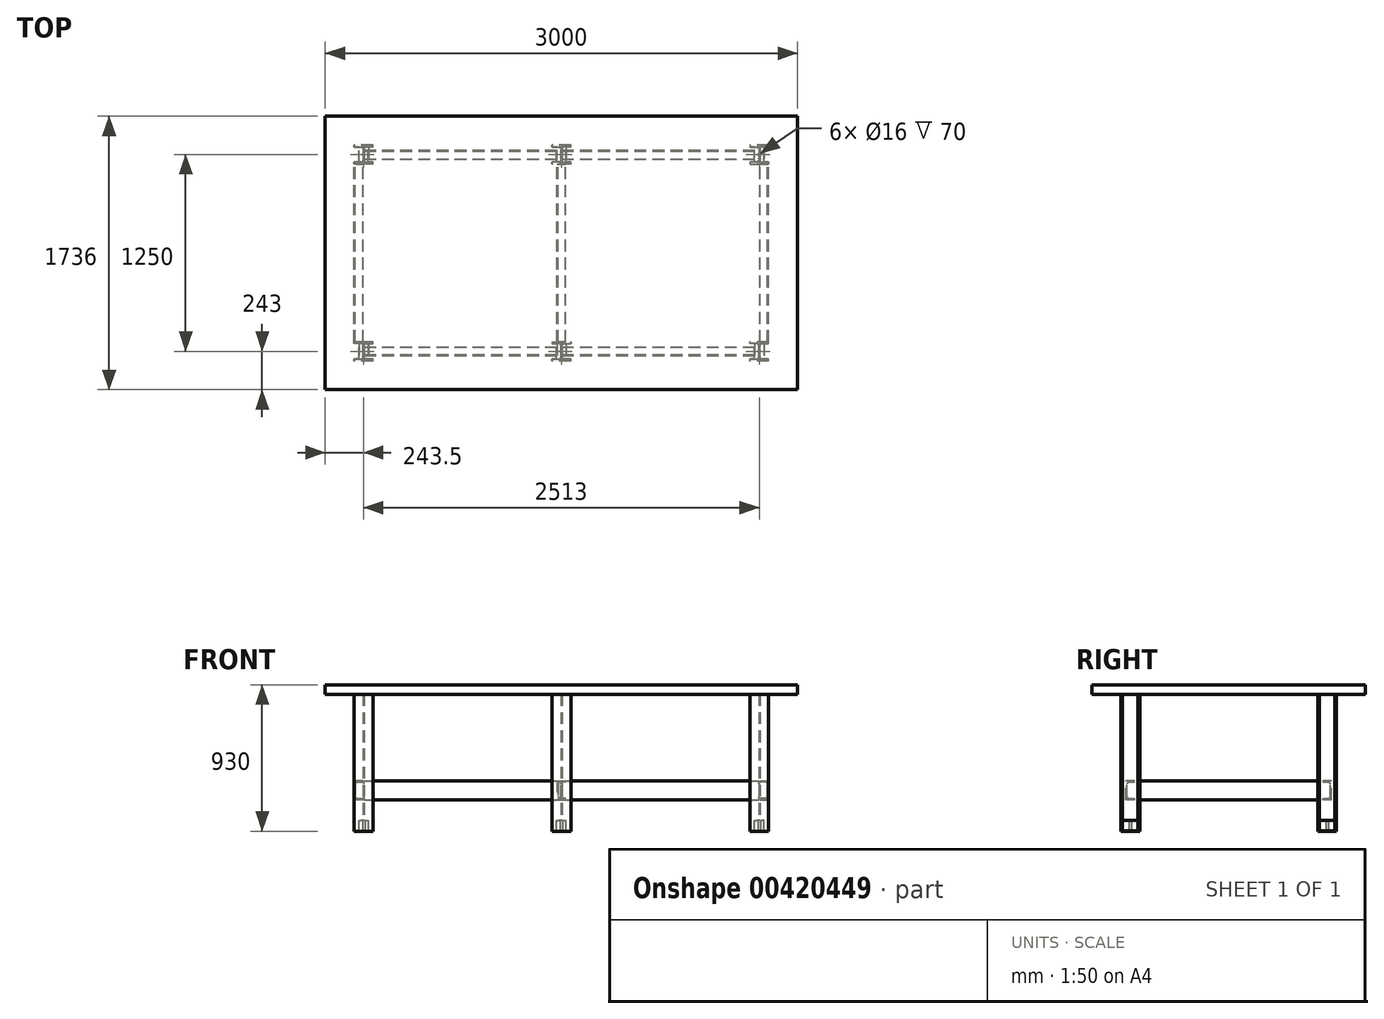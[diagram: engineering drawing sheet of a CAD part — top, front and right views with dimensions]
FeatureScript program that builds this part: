
annotation { "Feature Type Name" : "Feature", "Feature Type Description" : "" }
export const myFeature = defineFeature(function(context is Context, id is Id, definition is map)
    precondition{}
    {
        {
            var Q0;
            Q0=qCreatedBy(makeId("Top.planeOp"),FACE);
            var sketch = newSketch(context, id + "F0", { "sketchPlane" : qUnion([Q0])});
            skLineSegment(sketch, "E0", {"start": v(0, 60) * mm, "end": v(60, 60) * mm});
            skLineSegment(sketch, "E1", {"start": v(60, 60) * mm, "end": v(60, 49) * mm});
            skLineSegment(sketch, "E2", {"start": v(60, 49) * mm, "end": v(15.75, 49) * mm});
            skLineSegment(sketch, "E3", {"start": v(3.25, 36.5) * mm, "end": v(3.25, -36.5) * mm});
            skLineSegment(sketch, "E4", {"start": v(15.75, -49) * mm, "end": v(60, -49) * mm});
            skLineSegment(sketch, "E5", {"start": v(60, -49) * mm, "end": v(60, -60) * mm});
            skLineSegment(sketch, "E6", {"start": v(60, -60) * mm, "end": v(0, -60) * mm});
            skPoint(sketch, "E7.visualSharp", {"position": v(3.25, 49) * mm});
            skArc(sketch, "E7.filletArc", {"start": v(15.75, 49) * mm, "mid": v(6.91, 45.34) * mm, "end": v(3.25, 36.5) * mm});
            skPoint(sketch, "E8.visualSharp", {"position": v(3.25, -49) * mm});
            skArc(sketch, "E8.filletArc", {"start": v(3.25, -36.5) * mm, "mid": v(6.91, -45.34) * mm, "end": v(15.75, -49) * mm});
            skLineSegment(sketch, "E9.MirrorCS", {"start": v(0, 60) * mm, "end": v(-60, 60) * mm});
            skLineSegment(sketch, "E10.MirrorCS", {"start": v(-60, 60) * mm, "end": v(-60, 49) * mm});
            skPoint(sketch, "E11.MirrorP", {"position": v(-3.25, -49) * mm});
            skLineSegment(sketch, "E12.MirrorCS", {"start": v(-60, 49) * mm, "end": v(-15.75, 49) * mm});
            skLineSegment(sketch, "E13.MirrorCS", {"start": v(-3.25, 36.5) * mm, "end": v(-3.25, -36.5) * mm});
            skLineSegment(sketch, "E14.MirrorCS", {"start": v(-60, -49) * mm, "end": v(-60, -60) * mm});
            skLineSegment(sketch, "E15.MirrorCS", {"start": v(-60, -60) * mm, "end": v(0, -60) * mm});
            skArc(sketch, "E16.MirrorCS", {"start": v(-3.25, -36.5) * mm, "mid": v(-6.91, -45.34) * mm, "end": v(-15.75, -49) * mm});
            skLineSegment(sketch, "E17.MirrorCS", {"start": v(-15.75, -49) * mm, "end": v(-60, -49) * mm});
            skArc(sketch, "E18.MirrorCS", {"start": v(-15.75, 49) * mm, "mid": v(-6.91, 45.34) * mm, "end": v(-3.25, 36.5) * mm});
            skPoint(sketch, "E19.MirrorP", {"position": v(-3.25, 49) * mm});
            skLineSegment(sketch, "E20", {"start": v(-3.25, 0) * mm, "end": v(-1253.25, 0) * mm, "construction": true});
            skLineSegment(sketch, "E21.bottom", {"start": v(-2756.5, -1625) * mm, "end": v(243.5, -1625) * mm, "construction": true});
            skLineSegment(sketch, "E21.top", {"start": v(-2756.5, 375) * mm, "end": v(243.5, 375) * mm, "construction": true});
            skLineSegment(sketch, "E21.left", {"start": v(-2756.5, -1625) * mm, "end": v(-2756.5, 375) * mm, "construction": true});
            skLineSegment(sketch, "E21.right", {"start": v(243.5, -1625) * mm, "end": v(243.5, 375) * mm, "construction": true});
            skLineSegment(sketch, "E22", {"start": v(-628.25, 107.52) * mm, "end": v(-628.25, 0) * mm, "construction": true});
            skArc(sketch, "E23.MirrorCS", {"start": v(-1240.75, 49) * mm, "mid": v(-1249.59, 45.34) * mm, "end": v(-1253.25, 36.5) * mm});
            skArc(sketch, "E24.MirrorCS", {"start": v(-1272.25, 49) * mm, "mid": v(-1263.41, 45.34) * mm, "end": v(-1259.75, 36.5) * mm});
            skArc(sketch, "E25.MirrorCS", {"start": v(-1259.75, -36.5) * mm, "mid": v(-1263.41, -45.34) * mm, "end": v(-1272.25, -49) * mm});
            skLineSegment(sketch, "E26.MirrorCS", {"start": v(-1272.25, -49) * mm, "end": v(-1316.5, -49) * mm});
            skLineSegment(sketch, "E27.MirrorCS", {"start": v(-1256.5, 60) * mm, "end": v(-1316.5, 60) * mm});
            skLineSegment(sketch, "E28.MirrorCS", {"start": v(-1316.5, -49) * mm, "end": v(-1316.5, -60) * mm});
            skArc(sketch, "E29.MirrorCS", {"start": v(-1253.25, -36.5) * mm, "mid": v(-1249.59, -45.34) * mm, "end": v(-1240.75, -49) * mm});
            skLineSegment(sketch, "E30.MirrorCS", {"start": v(-1316.5, -60) * mm, "end": v(-1256.5, -60) * mm});
            skLineSegment(sketch, "E31.MirrorCS", {"start": v(-1316.5, 49) * mm, "end": v(-1272.25, 49) * mm});
            skLineSegment(sketch, "E32.MirrorCS", {"start": v(-1316.5, 60) * mm, "end": v(-1316.5, 49) * mm});
            skLineSegment(sketch, "E33.MirrorCS", {"start": v(-1196.5, -60) * mm, "end": v(-1256.5, -60) * mm});
            skLineSegment(sketch, "E34.MirrorCS", {"start": v(-1196.5, -49) * mm, "end": v(-1196.5, -60) * mm});
            skLineSegment(sketch, "E35.MirrorCS", {"start": v(-1240.75, -49) * mm, "end": v(-1196.5, -49) * mm});
            skLineSegment(sketch, "E36.MirrorCS", {"start": v(-1253.25, 36.5) * mm, "end": v(-1253.25, -36.5) * mm});
            skLineSegment(sketch, "E37.MirrorCS", {"start": v(-1196.5, 49) * mm, "end": v(-1240.75, 49) * mm});
            skLineSegment(sketch, "E38.MirrorCS", {"start": v(-1196.5, 60) * mm, "end": v(-1196.5, 49) * mm});
            skLineSegment(sketch, "E39.MirrorCS", {"start": v(-1256.5, 60) * mm, "end": v(-1196.5, 60) * mm});
            skLineSegment(sketch, "E40.MirrorCS", {"start": v(-1259.75, 36.5) * mm, "end": v(-1259.75, -36.5) * mm});
            skPoint(sketch, "E41.MirrorP", {"position": v(-1259.75, 49) * mm});
            skLineSegment(sketch, "E42.MirrorCS", {"start": v(-1253.25, 0) * mm, "end": v(-3.25, 0) * mm, "construction": true});
            skPoint(sketch, "E43.MirrorP", {"position": v(-1253.25, 49) * mm});
            skPoint(sketch, "E44.MirrorP", {"position": v(-1253.25, -49) * mm});
            skPoint(sketch, "E45.MirrorP", {"position": v(-1259.75, -49) * mm});
            skLineSegment(sketch, "E46", {"start": v(-1259.75, 0) * mm, "end": v(-2509.75, 0) * mm, "construction": true});
            skPoint(sketch, "E46.endSnap0", {"position": v(-1259.75, 0) * mm});
            skLineSegment(sketch, "E47", {"start": v(-1884.75, 66.72) * mm, "end": v(-1884.75, 0) * mm, "construction": true});
            skPoint(sketch, "E47.endSnap0", {"position": v(-1884.75, 0) * mm});
            skArc(sketch, "E48.MirrorCS", {"start": v(-2516.25, -36.5) * mm, "mid": v(-2519.91, -45.34) * mm, "end": v(-2528.75, -49) * mm});
            skArc(sketch, "E49.MirrorCS", {"start": v(-2509.75, -36.5) * mm, "mid": v(-2506.09, -45.34) * mm, "end": v(-2497.25, -49) * mm});
            skArc(sketch, "E50.MirrorCS", {"start": v(-2528.75, 49) * mm, "mid": v(-2519.91, 45.34) * mm, "end": v(-2516.25, 36.5) * mm});
            skLineSegment(sketch, "E51.MirrorCS", {"start": v(-2516.25, 36.5) * mm, "end": v(-2516.25, -36.5) * mm});
            skLineSegment(sketch, "E52.MirrorCS", {"start": v(-2509.75, 36.5) * mm, "end": v(-2509.75, -36.5) * mm});
            skArc(sketch, "E53.MirrorCS", {"start": v(-2497.25, 49) * mm, "mid": v(-2506.09, 45.34) * mm, "end": v(-2509.75, 36.5) * mm});
            skLineSegment(sketch, "E54.MirrorCS", {"start": v(-2497.25, -49) * mm, "end": v(-2453, -49) * mm});
            skLineSegment(sketch, "E55.MirrorCS", {"start": v(-2453, 49) * mm, "end": v(-2497.25, 49) * mm});
            skLineSegment(sketch, "E56.MirrorCS", {"start": v(-2453, -49) * mm, "end": v(-2453, -60) * mm});
            skLineSegment(sketch, "E57.MirrorCS", {"start": v(-2513, 60) * mm, "end": v(-2453, 60) * mm});
            skLineSegment(sketch, "E58.MirrorCS", {"start": v(-2513, 60) * mm, "end": v(-2573, 60) * mm});
            skLineSegment(sketch, "E59.MirrorCS", {"start": v(-2453, 60) * mm, "end": v(-2453, 49) * mm});
            skPoint(sketch, "E60.MirrorP", {"position": v(-2509.75, 0) * mm});
            skLineSegment(sketch, "E61.MirrorCS", {"start": v(-2453, -60) * mm, "end": v(-2513, -60) * mm});
            skLineSegment(sketch, "E62.MirrorCS", {"start": v(-2573, 49) * mm, "end": v(-2528.75, 49) * mm});
            skLineSegment(sketch, "E63.MirrorCS", {"start": v(-2573, 60) * mm, "end": v(-2573, 49) * mm});
            skLineSegment(sketch, "E64.MirrorCS", {"start": v(-2573, -60) * mm, "end": v(-2513, -60) * mm});
            skLineSegment(sketch, "E65.MirrorCS", {"start": v(-2573, -49) * mm, "end": v(-2573, -60) * mm});
            skLineSegment(sketch, "E66.MirrorCS", {"start": v(-2528.75, -49) * mm, "end": v(-2573, -49) * mm});
            skPoint(sketch, "E67.MirrorP", {"position": v(-2516.25, 49) * mm});
            skPoint(sketch, "E68.MirrorP", {"position": v(-2516.25, -49) * mm});
            skPoint(sketch, "E69.MirrorP", {"position": v(-2509.75, 49) * mm});
            skLineSegment(sketch, "E70.MirrorCS", {"start": v(-2509.75, 0) * mm, "end": v(-1259.75, 0) * mm, "construction": true});
            skPoint(sketch, "E71.MirrorP", {"position": v(-2509.75, -49) * mm});
            skLineSegment(sketch, "E72", {"start": v(-2573, -60) * mm, "end": v(-2573, -158.37) * mm, "construction": true});
            skLineSegment(sketch, "E73", {"start": v(-2573, -158.37) * mm, "end": v(60, -158.37) * mm, "construction": true});
            skLineSegment(sketch, "E74", {"start": v(60, -158.37) * mm, "end": v(60, -60) * mm, "construction": true});
            skLineSegment(sketch, "E75", {"start": v(-1256.5, -158.37) * mm, "end": v(-1256.5, -1625) * mm, "construction": true});
            skLineSegment(sketch, "E76", {"start": v(-2756.5, -625) * mm, "end": v(243.5, -625) * mm, "construction": true});
            skLineSegment(sketch, "E77.MirrorCS", {"start": v(-1253.25, -1286.5) * mm, "end": v(-1253.25, -1213.5) * mm});
            skLineSegment(sketch, "E78.MirrorCS", {"start": v(-1256.5, -1310) * mm, "end": v(-1196.5, -1310) * mm});
            skLineSegment(sketch, "E79.MirrorCS", {"start": v(-1196.5, -1299) * mm, "end": v(-1240.75, -1299) * mm});
            skArc(sketch, "E80.MirrorCS", {"start": v(-1259.75, -1213.5) * mm, "mid": v(-1263.41, -1204.66) * mm, "end": v(-1272.25, -1201) * mm});
            skArc(sketch, "E81.MirrorCS", {"start": v(-1240.75, -1299) * mm, "mid": v(-1249.59, -1295.34) * mm, "end": v(-1253.25, -1286.5) * mm});
            skArc(sketch, "E82.MirrorCS", {"start": v(-1253.25, -1213.5) * mm, "mid": v(-1249.59, -1204.66) * mm, "end": v(-1240.75, -1201) * mm});
            skLineSegment(sketch, "E83.MirrorCS", {"start": v(-1259.75, -1286.5) * mm, "end": v(-1259.75, -1213.5) * mm});
            skArc(sketch, "E84.MirrorCS", {"start": v(-1272.25, -1299) * mm, "mid": v(-1263.41, -1295.34) * mm, "end": v(-1259.75, -1286.5) * mm});
            skLineSegment(sketch, "E85.MirrorCS", {"start": v(-1196.5, -1190) * mm, "end": v(-1256.5, -1190) * mm});
            skLineSegment(sketch, "E86.MirrorCS", {"start": v(-1240.75, -1201) * mm, "end": v(-1196.5, -1201) * mm});
            skArc(sketch, "E87.MirrorCS", {"start": v(15.75, -1299) * mm, "mid": v(6.91, -1295.34) * mm, "end": v(3.25, -1286.5) * mm});
            skLineSegment(sketch, "E88.MirrorCS", {"start": v(0, -1310) * mm, "end": v(-60, -1310) * mm});
            skLineSegment(sketch, "E89.MirrorCS", {"start": v(-60, -1310) * mm, "end": v(-60, -1299) * mm});
            skLineSegment(sketch, "E90.MirrorCS", {"start": v(-60, -1201) * mm, "end": v(-60, -1190) * mm});
            skArc(sketch, "E91.MirrorCS", {"start": v(-3.25, -1213.5) * mm, "mid": v(-6.91, -1204.66) * mm, "end": v(-15.75, -1201) * mm});
            skLineSegment(sketch, "E92.MirrorCS", {"start": v(0, -1310) * mm, "end": v(60, -1310) * mm});
            skLineSegment(sketch, "E93.MirrorCS", {"start": v(60, -1299) * mm, "end": v(15.75, -1299) * mm});
            skLineSegment(sketch, "E94.MirrorCS", {"start": v(3.25, -1286.5) * mm, "end": v(3.25, -1213.5) * mm});
            skArc(sketch, "E95.MirrorCS", {"start": v(-15.75, -1299) * mm, "mid": v(-6.91, -1295.34) * mm, "end": v(-3.25, -1286.5) * mm});
            skArc(sketch, "E96.MirrorCS", {"start": v(-2516.25, -1213.5) * mm, "mid": v(-2519.91, -1204.66) * mm, "end": v(-2528.75, -1201) * mm});
            skLineSegment(sketch, "E97.MirrorCS", {"start": v(-3.25, -1286.5) * mm, "end": v(-3.25, -1213.5) * mm});
            skArc(sketch, "E98.MirrorCS", {"start": v(-2509.75, -1213.5) * mm, "mid": v(-2506.09, -1204.66) * mm, "end": v(-2497.25, -1201) * mm});
            skArc(sketch, "E99.MirrorCS", {"start": v(-2528.75, -1299) * mm, "mid": v(-2519.91, -1295.34) * mm, "end": v(-2516.25, -1286.5) * mm});
            skLineSegment(sketch, "E100.MirrorCS", {"start": v(-60, -1299) * mm, "end": v(-15.75, -1299) * mm});
            skLineSegment(sketch, "E101.MirrorCS", {"start": v(-15.75, -1201) * mm, "end": v(-60, -1201) * mm});
            skLineSegment(sketch, "E102.MirrorCS", {"start": v(-2453, -1190) * mm, "end": v(-2513, -1190) * mm});
            skArc(sketch, "E103.MirrorCS", {"start": v(3.25, -1213.5) * mm, "mid": v(6.91, -1204.66) * mm, "end": v(15.75, -1201) * mm});
            skLineSegment(sketch, "E104.MirrorCS", {"start": v(-2516.25, -1286.5) * mm, "end": v(-2516.25, -1213.5) * mm});
            skLineSegment(sketch, "E105.MirrorCS", {"start": v(-1256.5, -1310) * mm, "end": v(-1316.5, -1310) * mm});
            skLineSegment(sketch, "E106.MirrorCS", {"start": v(-2497.25, -1201) * mm, "end": v(-2453, -1201) * mm});
            skLineSegment(sketch, "E107.MirrorCS", {"start": v(-2573, -1201) * mm, "end": v(-2573, -1190) * mm});
            skLineSegment(sketch, "E108.MirrorCS", {"start": v(-1272.25, -1201) * mm, "end": v(-1316.5, -1201) * mm});
            skLineSegment(sketch, "E109.MirrorCS", {"start": v(-2513, -1310) * mm, "end": v(-2453, -1310) * mm});
            skLineSegment(sketch, "E110.MirrorCS", {"start": v(-60, -1190) * mm, "end": v(0, -1190) * mm});
            skLineSegment(sketch, "E111.MirrorCS", {"start": v(-2509.75, -1286.5) * mm, "end": v(-2509.75, -1213.5) * mm});
            skLineSegment(sketch, "E112.MirrorCS", {"start": v(15.75, -1201) * mm, "end": v(60, -1201) * mm});
            skLineSegment(sketch, "E113.MirrorCS", {"start": v(-2573, -1299) * mm, "end": v(-2528.75, -1299) * mm});
            skLineSegment(sketch, "E114.MirrorCS", {"start": v(60, -1190) * mm, "end": v(0, -1190) * mm});
            skLineSegment(sketch, "E115.MirrorCS", {"start": v(-1316.5, -1299) * mm, "end": v(-1272.25, -1299) * mm});
            skArc(sketch, "E116.MirrorCS", {"start": v(-2497.25, -1299) * mm, "mid": v(-2506.09, -1295.34) * mm, "end": v(-2509.75, -1286.5) * mm});
            skLineSegment(sketch, "E117.MirrorCS", {"start": v(-2573, -1190) * mm, "end": v(-2513, -1190) * mm});
            skLineSegment(sketch, "E118.MirrorCS", {"start": v(-1316.5, -1201) * mm, "end": v(-1316.5, -1190) * mm});
            skLineSegment(sketch, "E119.MirrorCS", {"start": v(-2453, -1299) * mm, "end": v(-2497.25, -1299) * mm});
            skLineSegment(sketch, "E120.MirrorCS", {"start": v(-2573, -1310) * mm, "end": v(-2573, -1299) * mm});
            skLineSegment(sketch, "E121.MirrorCS", {"start": v(-2513, -1310) * mm, "end": v(-2573, -1310) * mm});
            skLineSegment(sketch, "E122.MirrorCS", {"start": v(-1316.5, -1190) * mm, "end": v(-1256.5, -1190) * mm});
            skLineSegment(sketch, "E123.MirrorCS", {"start": v(-1316.5, -1310) * mm, "end": v(-1316.5, -1299) * mm});
            skLineSegment(sketch, "E124.MirrorCS", {"start": v(-2453, -1201) * mm, "end": v(-2453, -1190) * mm});
            skLineSegment(sketch, "E125.MirrorCS", {"start": v(-2528.75, -1201) * mm, "end": v(-2573, -1201) * mm});
            skLineSegment(sketch, "E126.MirrorCS", {"start": v(-2453, -1310) * mm, "end": v(-2453, -1299) * mm});
            skLineSegment(sketch, "E127.MirrorCS", {"start": v(60, -1201) * mm, "end": v(60, -1190) * mm});
            skLineSegment(sketch, "E128.MirrorCS", {"start": v(60, -1310) * mm, "end": v(60, -1299) * mm});
            skLineSegment(sketch, "E129.MirrorCS", {"start": v(-1196.5, -1310) * mm, "end": v(-1196.5, -1299) * mm});
            skLineSegment(sketch, "E130.MirrorCS", {"start": v(-1196.5, -1201) * mm, "end": v(-1196.5, -1190) * mm});
            skLineSegment(sketch, "E131.MirrorCS", {"start": v(-2573, -1190) * mm, "end": v(-2573, -1091.63) * mm, "construction": true});
            skLineSegment(sketch, "E132.MirrorCS", {"start": v(60, -1091.63) * mm, "end": v(60, -1190) * mm, "construction": true});
            skPoint(sketch, "E133.MirrorP", {"position": v(-1259.75, -1250) * mm});
            skPoint(sketch, "E134.MirrorP", {"position": v(-1253.25, -1201) * mm});
            skPoint(sketch, "E135.MirrorP", {"position": v(-2509.75, -1250) * mm});
            skLineSegment(sketch, "E136.MirrorCS", {"start": v(-1253.25, -1250) * mm, "end": v(-3.25, -1250) * mm, "construction": true});
            skPoint(sketch, "E137.MirrorP", {"position": v(-2509.75, -1299) * mm});
            skPoint(sketch, "E138.MirrorP", {"position": v(-1259.75, -1299) * mm});
            skPoint(sketch, "E139.MirrorP", {"position": v(3.25, -1299) * mm});
            skLineSegment(sketch, "E140.MirrorCS", {"start": v(-1259.75, -1250) * mm, "end": v(-2509.75, -1250) * mm, "construction": true});
            skPoint(sketch, "E141.MirrorP", {"position": v(-2509.75, -1201) * mm});
            skPoint(sketch, "E142.MirrorP", {"position": v(-3.25, -1299) * mm});
            skPoint(sketch, "E143.MirrorP", {"position": v(-1253.25, -1299) * mm});
            skLineSegment(sketch, "E144.MirrorCS", {"start": v(-2509.75, -1250) * mm, "end": v(-1259.75, -1250) * mm, "construction": true});
            skLineSegment(sketch, "E145.MirrorCS", {"start": v(-2573, -1091.63) * mm, "end": v(60, -1091.63) * mm, "construction": true});
            skPoint(sketch, "E146.MirrorP", {"position": v(-2516.25, -1299) * mm});
            skPoint(sketch, "E147.MirrorP", {"position": v(-2516.25, -1201) * mm});
            skLineSegment(sketch, "E148.MirrorCS", {"start": v(-628.25, -1357.52) * mm, "end": v(-628.25, -1250) * mm, "construction": true});
            skLineSegment(sketch, "E149.MirrorCS", {"start": v(-3.25, -1250) * mm, "end": v(-1253.25, -1250) * mm, "construction": true});
            skPoint(sketch, "E150.MirrorP", {"position": v(3.25, -1201) * mm});
            skLineSegment(sketch, "E151.MirrorCS", {"start": v(243.5, 375) * mm, "end": v(243.5, -1625) * mm, "construction": true});
            skLineSegment(sketch, "E152.MirrorCS", {"start": v(-1884.75, -1316.72) * mm, "end": v(-1884.75, -1250) * mm, "construction": true});
            skPoint(sketch, "E153.MirrorP", {"position": v(-3.25, -1201) * mm});
            skLineSegment(sketch, "E154.MirrorCS", {"start": v(-1256.5, -1091.63) * mm, "end": v(-1256.5, 375) * mm, "construction": true});
            skPoint(sketch, "E155.MirrorP", {"position": v(-1259.75, -1201) * mm});
            skPoint(sketch, "E156.MirrorP", {"position": v(-1884.75, -1250) * mm});
            skSolve(sketch);
        }
        {
            var Q0;
            Q0 = qSketchRegion(id + "F0", true);
            extrude(context, id + "F1", {"entities" : qUnion([Q0]), "depth" : 800 * mm});
        }
        {
            var Q0;
            Q0=makeQuery(id+"F1.opExtrude","CAP_FACE",FACE,{"disambiguationData":[OSD([sQuery(id+"F0.wireOp",EDGE,"E0"),sQuery(id+"F0.wireOp",EDGE,"E1"),sQuery(id+"F0.wireOp",EDGE,"E2"),sQuery(id+"F0.wireOp",EDGE,"E3"),sQuery(id+"F0.wireOp",EDGE,"E4"),sQuery(id+"F0.wireOp",EDGE,"E5"),sQuery(id+"F0.wireOp",EDGE,"E6"),sQuery(id+"F0.wireOp",EDGE,"E7.filletArc"),sQuery(id+"F0.wireOp",EDGE,"E8.filletArc"),sQuery(id+"F0.wireOp",EDGE,"E9.MirrorCS"),sQuery(id+"F0.wireOp",EDGE,"E10.MirrorCS"),sQuery(id+"F0.wireOp",EDGE,"E12.MirrorCS"),sQuery(id+"F0.wireOp",EDGE,"E13.MirrorCS"),sQuery(id+"F0.wireOp",EDGE,"E14.MirrorCS"),sQuery(id+"F0.wireOp",EDGE,"E15.MirrorCS"),sQuery(id+"F0.wireOp",EDGE,"E16.MirrorCS"),sQuery(id+"F0.wireOp",EDGE,"E17.MirrorCS"),sQuery(id+"F0.wireOp",EDGE,"E18.MirrorCS")])],"isStart":true});
            var sketch = newSketch(context, id + "F2", { "sketchPlane" : qUnion([Q0])});
            skLineSegment(sketch, "E157.bottom", {"start": v(-60, 60) * mm, "end": v(60, 60) * mm});
            skLineSegment(sketch, "E157.top", {"start": v(-60, 49) * mm, "end": v(60, 49) * mm});
            skLineSegment(sketch, "E157.left", {"start": v(-60, 60) * mm, "end": v(-60, 49) * mm});
            skLineSegment(sketch, "E157.right", {"start": v(60, 60) * mm, "end": v(60, 49) * mm});
            skLineSegment(sketch, "E158.bottom", {"start": v(-60, -60) * mm, "end": v(60, -60) * mm});
            skLineSegment(sketch, "E158.top", {"start": v(-60, -49) * mm, "end": v(60, -49) * mm});
            skLineSegment(sketch, "E158.left", {"start": v(-60, -60) * mm, "end": v(-60, -49) * mm});
            skLineSegment(sketch, "E158.right", {"start": v(60, -60) * mm, "end": v(60, -49) * mm});
            skSolve(sketch);
        }
        {
            var Q0;
            Q0=makeQuery(id+"F2.imprint","IMPRINT",FACE,{"disambiguationData":[TD([[makeQuery(id+"F2.imprint","IMPRINT",EDGE,{"derivedFrom":makeQuery(id+"F1.opExtrude","CAP_EDGE",EDGE,{"disambiguationData":[OSD([sQuery(id+"F0.wireOp",EDGE,"E3")])],"isStart":true})}),1.0]])]});
            var sketch = newSketch(context, id + "F3", { "sketchPlane" : qUnion([Q0])});
            skLineSegment(sketch, "E159.bottom", {"start": v(30, 49) * mm, "end": v(-30, 49) * mm});
            skLineSegment(sketch, "E159.top", {"start": v(30, -49) * mm, "end": v(-30, -49) * mm});
            skLineSegment(sketch, "E159.left", {"start": v(30, 49) * mm, "end": v(30, -49) * mm});
            skLineSegment(sketch, "E159.right", {"start": v(-30, 49) * mm, "end": v(-30, -49) * mm});
            skLineSegment(sketch, "E160.bottom", {"start": v(-1286.5, -49) * mm, "end": v(-1226.5, -49) * mm});
            skLineSegment(sketch, "E160.top", {"start": v(-1286.5, 49) * mm, "end": v(-1226.5, 49) * mm});
            skLineSegment(sketch, "E160.left", {"start": v(-1286.5, -49) * mm, "end": v(-1286.5, 49) * mm});
            skLineSegment(sketch, "E160.right", {"start": v(-1226.5, -49) * mm, "end": v(-1226.5, 49) * mm});
            skLineSegment(sketch, "E161.bottom", {"start": v(-2543, -49) * mm, "end": v(-2483, -49) * mm});
            skLineSegment(sketch, "E161.top", {"start": v(-2543, 49) * mm, "end": v(-2483, 49) * mm});
            skLineSegment(sketch, "E161.left", {"start": v(-2543, -49) * mm, "end": v(-2543, 49) * mm});
            skLineSegment(sketch, "E161.right", {"start": v(-2483, -49) * mm, "end": v(-2483, 49) * mm});
            skLineSegment(sketch, "E162.bottom", {"start": v(-2543, 1201) * mm, "end": v(-2483, 1201) * mm});
            skLineSegment(sketch, "E162.top", {"start": v(-2543, 1299) * mm, "end": v(-2483, 1299) * mm});
            skLineSegment(sketch, "E162.left", {"start": v(-2543, 1201) * mm, "end": v(-2543, 1299) * mm});
            skLineSegment(sketch, "E162.right", {"start": v(-2483, 1201) * mm, "end": v(-2483, 1299) * mm});
            skLineSegment(sketch, "E163.bottom", {"start": v(-1286.5, 1201) * mm, "end": v(-1226.5, 1201) * mm});
            skLineSegment(sketch, "E163.top", {"start": v(-1286.5, 1299) * mm, "end": v(-1226.5, 1299) * mm});
            skLineSegment(sketch, "E163.left", {"start": v(-1286.5, 1201) * mm, "end": v(-1286.5, 1299) * mm});
            skLineSegment(sketch, "E163.right", {"start": v(-1226.5, 1201) * mm, "end": v(-1226.5, 1299) * mm});
            skLineSegment(sketch, "E164.bottom", {"start": v(-30, 1201) * mm, "end": v(30, 1201) * mm});
            skLineSegment(sketch, "E164.top", {"start": v(-30, 1299) * mm, "end": v(30, 1299) * mm});
            skLineSegment(sketch, "E164.left", {"start": v(-30, 1201) * mm, "end": v(-30, 1299) * mm});
            skLineSegment(sketch, "E164.right", {"start": v(30, 1201) * mm, "end": v(30, 1299) * mm});
            skSolve(sketch);
        }
        {
            var Q0;
            Q0 = qSketchRegion(id + "F3", true);
            extrude(context, id + "F4", {"entities" : qUnion([Q0]), "depth" : 70 * mm});
        }
        {
            var Q0;
            Q0=makeQuery(id+"F2.imprint","IMPRINT",FACE,{"disambiguationData":[TD([[makeQuery(id+"F2.imprint","IMPRINT",EDGE,{"derivedFrom":sQuery(id+"F2.wireOp",EDGE,"E157.bottom")}),-1.0]])]});
            var sketch = newSketch(context, id + "F5", { "sketchPlane" : qUnion([Q0])});
            skLineSegment(sketch, "E165.bottom", {"start": v(60, -60) * mm, "end": v(-60, -60) * mm});
            skLineSegment(sketch, "E165.top", {"start": v(60, -49) * mm, "end": v(-60, -49) * mm});
            skLineSegment(sketch, "E165.left", {"start": v(60, -60) * mm, "end": v(60, -49) * mm});
            skLineSegment(sketch, "E165.right", {"start": v(-60, -60) * mm, "end": v(-60, -49) * mm});
            skLineSegment(sketch, "E166.bottom", {"start": v(60, 49) * mm, "end": v(-60, 49) * mm});
            skLineSegment(sketch, "E166.top", {"start": v(60, 60) * mm, "end": v(-60, 60) * mm});
            skLineSegment(sketch, "E166.left", {"start": v(60, 49) * mm, "end": v(60, 60) * mm});
            skLineSegment(sketch, "E166.right", {"start": v(-60, 49) * mm, "end": v(-60, 60) * mm});
            skLineSegment(sketch, "E167.bottom", {"start": v(-1196.5, 60) * mm, "end": v(-1316.5, 60) * mm});
            skLineSegment(sketch, "E167.top", {"start": v(-1196.5, 49) * mm, "end": v(-1316.5, 49) * mm});
            skLineSegment(sketch, "E167.left", {"start": v(-1196.5, 60) * mm, "end": v(-1196.5, 49) * mm});
            skLineSegment(sketch, "E167.right", {"start": v(-1316.5, 60) * mm, "end": v(-1316.5, 49) * mm});
            skLineSegment(sketch, "E168.bottom", {"start": v(-1196.5, -49) * mm, "end": v(-1316.5, -49) * mm});
            skLineSegment(sketch, "E168.top", {"start": v(-1196.5, -60) * mm, "end": v(-1316.5, -60) * mm});
            skLineSegment(sketch, "E168.left", {"start": v(-1196.5, -49) * mm, "end": v(-1196.5, -60) * mm});
            skLineSegment(sketch, "E168.right", {"start": v(-1316.5, -49) * mm, "end": v(-1316.5, -60) * mm});
            skLineSegment(sketch, "E169.bottom", {"start": v(-2453, 60) * mm, "end": v(-2573, 60) * mm});
            skLineSegment(sketch, "E169.top", {"start": v(-2453, 49) * mm, "end": v(-2573, 49) * mm});
            skLineSegment(sketch, "E169.left", {"start": v(-2453, 60) * mm, "end": v(-2453, 49) * mm});
            skLineSegment(sketch, "E169.right", {"start": v(-2573, 60) * mm, "end": v(-2573, 49) * mm});
            skLineSegment(sketch, "E170.bottom", {"start": v(-2453, -49) * mm, "end": v(-2573, -49) * mm});
            skLineSegment(sketch, "E170.top", {"start": v(-2453, -60) * mm, "end": v(-2573, -60) * mm});
            skLineSegment(sketch, "E170.left", {"start": v(-2453, -49) * mm, "end": v(-2453, -60) * mm});
            skLineSegment(sketch, "E170.right", {"start": v(-2573, -49) * mm, "end": v(-2573, -60) * mm});
            skLineSegment(sketch, "E171.bottom", {"start": v(-2453, 1310) * mm, "end": v(-2573, 1310) * mm});
            skLineSegment(sketch, "E171.top", {"start": v(-2453, 1299) * mm, "end": v(-2573, 1299) * mm});
            skLineSegment(sketch, "E171.left", {"start": v(-2453, 1310) * mm, "end": v(-2453, 1299) * mm});
            skLineSegment(sketch, "E171.right", {"start": v(-2573, 1310) * mm, "end": v(-2573, 1299) * mm});
            skLineSegment(sketch, "E172.bottom", {"start": v(-2453, 1201) * mm, "end": v(-2573, 1201) * mm});
            skLineSegment(sketch, "E172.top", {"start": v(-2453, 1190) * mm, "end": v(-2573, 1190) * mm});
            skLineSegment(sketch, "E172.left", {"start": v(-2453, 1201) * mm, "end": v(-2453, 1190) * mm});
            skLineSegment(sketch, "E172.right", {"start": v(-2573, 1201) * mm, "end": v(-2573, 1190) * mm});
            skLineSegment(sketch, "E173.bottom", {"start": v(-1196.5, 1310) * mm, "end": v(-1316.5, 1310) * mm});
            skLineSegment(sketch, "E173.top", {"start": v(-1196.5, 1299) * mm, "end": v(-1316.5, 1299) * mm});
            skLineSegment(sketch, "E173.left", {"start": v(-1196.5, 1310) * mm, "end": v(-1196.5, 1299) * mm});
            skLineSegment(sketch, "E173.right", {"start": v(-1316.5, 1310) * mm, "end": v(-1316.5, 1299) * mm});
            skLineSegment(sketch, "E174.bottom", {"start": v(60, 1310) * mm, "end": v(-60, 1310) * mm});
            skLineSegment(sketch, "E174.top", {"start": v(60, 1299) * mm, "end": v(-60, 1299) * mm});
            skLineSegment(sketch, "E174.left", {"start": v(60, 1310) * mm, "end": v(60, 1299) * mm});
            skLineSegment(sketch, "E174.right", {"start": v(-60, 1310) * mm, "end": v(-60, 1299) * mm});
            skLineSegment(sketch, "E175.bottom", {"start": v(60, 1201) * mm, "end": v(-60, 1201) * mm});
            skLineSegment(sketch, "E175.top", {"start": v(60, 1190) * mm, "end": v(-60, 1190) * mm});
            skLineSegment(sketch, "E175.left", {"start": v(60, 1201) * mm, "end": v(60, 1190) * mm});
            skLineSegment(sketch, "E175.right", {"start": v(-60, 1201) * mm, "end": v(-60, 1190) * mm});
            skLineSegment(sketch, "E176.bottom", {"start": v(-1316.5, 1190) * mm, "end": v(-1196.5, 1190) * mm});
            skLineSegment(sketch, "E176.top", {"start": v(-1316.5, 1201) * mm, "end": v(-1196.5, 1201) * mm});
            skLineSegment(sketch, "E176.left", {"start": v(-1316.5, 1190) * mm, "end": v(-1316.5, 1201) * mm});
            skLineSegment(sketch, "E176.right", {"start": v(-1196.5, 1190) * mm, "end": v(-1196.5, 1201) * mm});
            skSolve(sketch);
        }
        {
            var Q0;
            Q0 = qSketchRegion(id + "F5", true);
            extrude(context, id + "F6", {"entities" : qUnion([Q0]), "operationType" : NewBodyOperationType.ADD, "depth" : 70 * mm});
        }
        {
            var Q0;
            Q0=makeQuery(id+"F4.opExtrude","CAP_FACE",FACE,{"disambiguationData":[OSD([sQuery(id+"F3.wireOp",EDGE,"E159.bottom"),sQuery(id+"F3.wireOp",EDGE,"E159.top"),sQuery(id+"F3.wireOp",EDGE,"E159.left"),sQuery(id+"F3.wireOp",EDGE,"E159.right")])],"isStart":false});
            var sketch = newSketch(context, id + "F7", { "sketchPlane" : qUnion([Q0])});
            skCircle(sketch, "E177", {"center": v(0, 0) * mm, "radius": 8 * mm});
            skCircle(sketch, "E178", {"center": v(0, 1250) * mm, "radius": 8 * mm});
            skCircle(sketch, "E179", {"center": v(-1256.5, 1250) * mm, "radius": 8 * mm});
            skCircle(sketch, "E180", {"center": v(-2513, 1250) * mm, "radius": 8 * mm});
            skCircle(sketch, "E181", {"center": v(-2513, 0) * mm, "radius": 8 * mm});
            skCircle(sketch, "E182", {"center": v(-1256.5, 0) * mm, "radius": 8 * mm});
            skSolve(sketch);
        }
        {
            var Q0;
            Q0 = qSketchRegion(id + "F7", true);
            extrude(context, id + "F8", {"entities" : qUnion([Q0]), "operationType" : NewBodyOperationType.REMOVE, "oppositeDirection" : true, "depth" : 70 * mm});
        }
        {
            var Q0;
            Q0=makeQuery(id+"F4.opExtrude","CAP_EDGE",EDGE,{"disambiguationData":[OSD([sQuery(id+"F3.wireOp",EDGE,"E159.left")])],"isStart":true});
            var Q1;
            Q1=makeQuery(id+"F4.opExtrude","CAP_EDGE",EDGE,{"disambiguationData":[OSD([sQuery(id+"F3.wireOp",EDGE,"E159.left")])],"isStart":false});
            var Q2;
            Q2=makeQuery(id+"F4.opExtrude","CAP_EDGE",EDGE,{"disambiguationData":[OSD([sQuery(id+"F3.wireOp",EDGE,"E159.right")])],"isStart":false});
            var Q3;
            Q3=makeQuery(id+"F4.opExtrude","CAP_EDGE",EDGE,{"disambiguationData":[OSD([sQuery(id+"F3.wireOp",EDGE,"E159.right")])],"isStart":true});
            var Q4;
            Q4=makeQuery(id+"F4.opExtrude","CAP_EDGE",EDGE,{"disambiguationData":[OSD([sQuery(id+"F3.wireOp",EDGE,"E160.right")])],"isStart":true});
            var Q5;
            Q5=makeQuery(id+"F4.opExtrude","CAP_EDGE",EDGE,{"disambiguationData":[OSD([sQuery(id+"F3.wireOp",EDGE,"E160.right")])],"isStart":false});
            var Q6;
            Q6=makeQuery(id+"F4.opExtrude","CAP_EDGE",EDGE,{"disambiguationData":[OSD([sQuery(id+"F3.wireOp",EDGE,"E160.left")])],"isStart":false});
            var Q7;
            Q7=makeQuery(id+"F4.opExtrude","CAP_EDGE",EDGE,{"disambiguationData":[OSD([sQuery(id+"F3.wireOp",EDGE,"E160.left")])],"isStart":true});
            var Q8;
            Q8=makeQuery(id+"F4.opExtrude","CAP_EDGE",EDGE,{"disambiguationData":[OSD([sQuery(id+"F3.wireOp",EDGE,"E161.left")])],"isStart":true});
            var Q9;
            Q9=makeQuery(id+"F4.opExtrude","CAP_EDGE",EDGE,{"disambiguationData":[OSD([sQuery(id+"F3.wireOp",EDGE,"E161.left")])],"isStart":false});
            var Q10;
            Q10=makeQuery(id+"F4.opExtrude","CAP_EDGE",EDGE,{"disambiguationData":[OSD([sQuery(id+"F3.wireOp",EDGE,"E161.right")])],"isStart":false});
            var Q11;
            Q11=makeQuery(id+"F4.opExtrude","CAP_EDGE",EDGE,{"disambiguationData":[OSD([sQuery(id+"F3.wireOp",EDGE,"E161.right")])],"isStart":true});
            var Q12;
            Q12=makeQuery(id+"F4.opExtrude","CAP_EDGE",EDGE,{"disambiguationData":[OSD([sQuery(id+"F3.wireOp",EDGE,"E164.right")])],"isStart":true});
            var Q13;
            Q13=makeQuery(id+"F4.opExtrude","CAP_EDGE",EDGE,{"disambiguationData":[OSD([sQuery(id+"F3.wireOp",EDGE,"E164.right")])],"isStart":false});
            var Q14;
            Q14=makeQuery(id+"F4.opExtrude","CAP_EDGE",EDGE,{"disambiguationData":[OSD([sQuery(id+"F3.wireOp",EDGE,"E164.left")])],"isStart":false});
            var Q15;
            Q15=makeQuery(id+"F4.opExtrude","CAP_EDGE",EDGE,{"disambiguationData":[OSD([sQuery(id+"F3.wireOp",EDGE,"E164.left")])],"isStart":true});
            var Q16;
            Q16=makeQuery(id+"F4.opExtrude","CAP_EDGE",EDGE,{"disambiguationData":[OSD([sQuery(id+"F3.wireOp",EDGE,"E163.left")])],"isStart":true});
            var Q17;
            Q17=makeQuery(id+"F4.opExtrude","CAP_EDGE",EDGE,{"disambiguationData":[OSD([sQuery(id+"F3.wireOp",EDGE,"E163.left")])],"isStart":false});
            var Q18;
            Q18=makeQuery(id+"F4.opExtrude","CAP_EDGE",EDGE,{"disambiguationData":[OSD([sQuery(id+"F3.wireOp",EDGE,"E163.right")])],"isStart":false});
            var Q19;
            Q19=makeQuery(id+"F4.opExtrude","CAP_EDGE",EDGE,{"disambiguationData":[OSD([sQuery(id+"F3.wireOp",EDGE,"E163.right")])],"isStart":true});
            var Q20;
            Q20=makeQuery(id+"F4.opExtrude","CAP_EDGE",EDGE,{"disambiguationData":[OSD([sQuery(id+"F3.wireOp",EDGE,"E162.right")])],"isStart":true});
            var Q21;
            Q21=makeQuery(id+"F4.opExtrude","CAP_EDGE",EDGE,{"disambiguationData":[OSD([sQuery(id+"F3.wireOp",EDGE,"E162.right")])],"isStart":false});
            var Q22;
            Q22=makeQuery(id+"F4.opExtrude","CAP_EDGE",EDGE,{"disambiguationData":[OSD([sQuery(id+"F3.wireOp",EDGE,"E162.left")])],"isStart":false});
            var Q23;
            Q23=makeQuery(id+"F4.opExtrude","CAP_EDGE",EDGE,{"disambiguationData":[OSD([sQuery(id+"F3.wireOp",EDGE,"E162.left")])],"isStart":true});
            chamfer(context, id + "F9", {"entities" : qUnion([Q0, Q1, Q2, Q3, Q4, Q5, Q6, Q7, Q8, Q9, Q10, Q11, Q12, Q13, Q14, Q15, Q16, Q17, Q18, Q19, Q20, Q21, Q22, Q23]), "width" : 1 * mm, "tangentPropagation" : true});
        }
        {
            var Q0;
            Q0=makeQuery(id+"F1.opExtrude","SWEPT_FACE",FACE,{"disambiguationData":[OSD([sQuery(id+"F0.wireOp",EDGE,"E97.MirrorCS")])]});
            var sketch = newSketch(context, id + "F10", { "sketchPlane" : qUnion([Q0])});
            skLineSegment(sketch, "E183", {"start": v(1222.5, 250) * mm, "end": v(1277.5, 250) * mm});
            skLineSegment(sketch, "E184", {"start": v(1277.5, 250) * mm, "end": v(1277.5, 130) * mm});
            skLineSegment(sketch, "E185", {"start": v(1277.5, 130) * mm, "end": v(1222.5, 130) * mm});
            skLineSegment(sketch, "E186", {"start": v(1222.5, 250) * mm, "end": v(1222.5, 247.45) * mm});
            skLineSegment(sketch, "E187", {"start": v(1226.62, 242.97) * mm, "end": v(1262.26, 239.97) * mm});
            skLineSegment(sketch, "E188", {"start": v(1270.5, 231) * mm, "end": v(1270.5, 149) * mm});
            skLineSegment(sketch, "E189", {"start": v(1262.26, 140.03) * mm, "end": v(1226.62, 137.03) * mm});
            skLineSegment(sketch, "E190", {"start": v(1222.5, 132.55) * mm, "end": v(1222.5, 130) * mm});
            skPoint(sketch, "E191.visualSharp", {"position": v(1270.5, 239.27) * mm});
            skArc(sketch, "E191.filletArc", {"start": v(1270.5, 231) * mm, "mid": v(1268.13, 237.1) * mm, "end": v(1262.26, 239.97) * mm});
            skPoint(sketch, "E192.visualSharp", {"position": v(1270.5, 140.73) * mm});
            skArc(sketch, "E192.filletArc", {"start": v(1262.26, 140.03) * mm, "mid": v(1268.13, 142.9) * mm, "end": v(1270.5, 149) * mm});
            skLineSegment(sketch, "E193", {"start": v(1250, 250) * mm, "end": v(1250, 241) * mm, "construction": true});
            skLineSegment(sketch, "E194.trimOffspring", {"start": v(1250, 139) * mm, "end": v(1250, 130) * mm, "construction": true});
            skPoint(sketch, "E195.visualSharp", {"position": v(1222.5, 243.32) * mm});
            skArc(sketch, "E195.filletArc", {"start": v(1222.5, 247.45) * mm, "mid": v(1223.69, 244.4) * mm, "end": v(1226.62, 242.97) * mm});
            skPoint(sketch, "E196.visualSharp", {"position": v(1222.5, 136.68) * mm});
            skArc(sketch, "E196.filletArc", {"start": v(1226.62, 137.03) * mm, "mid": v(1223.69, 135.6) * mm, "end": v(1222.5, 132.55) * mm});
            skLineSegment(sketch, "E197", {"start": v(1250, 800) * mm, "end": v(1250, -101.35) * mm, "construction": true});
            skLineSegment(sketch, "E198", {"start": v(1270.5, 190) * mm, "end": v(1277.5, 190) * mm});
            skPoint(sketch, "E198.endSnap0", {"position": v(1277.5, 190) * mm});
            skLineSegment(sketch, "E199", {"start": v(0, 805.38) * mm, "end": v(0, -67.6) * mm, "construction": true});
            skLineSegment(sketch, "E200", {"start": v(0, 805.38) * mm, "end": v(1250, 805.38) * mm, "construction": true});
            skLineSegment(sketch, "E201", {"start": v(1250, 800) * mm, "end": v(1250, 805.38) * mm, "construction": true});
            skLineSegment(sketch, "E202", {"start": v(625, 805.38) * mm, "end": v(625, -110.92) * mm, "construction": true});
            skLineSegment(sketch, "E203.MirrorCS", {"start": v(27.5, 250) * mm, "end": v(27.5, 247.45) * mm});
            skArc(sketch, "E204.MirrorCS", {"start": v(27.5, 247.45) * mm, "mid": v(26.31, 244.4) * mm, "end": v(23.38, 242.97) * mm});
            skLineSegment(sketch, "E205.MirrorCS", {"start": v(0, 250) * mm, "end": v(0, 241) * mm, "construction": true});
            skLineSegment(sketch, "E206.MirrorCS", {"start": v(23.38, 242.97) * mm, "end": v(-12.26, 239.97) * mm});
            skLineSegment(sketch, "E207.MirrorCS", {"start": v(27.5, 132.55) * mm, "end": v(27.5, 130) * mm});
            skArc(sketch, "E208.MirrorCS", {"start": v(23.38, 137.03) * mm, "mid": v(26.31, 135.6) * mm, "end": v(27.5, 132.55) * mm});
            skLineSegment(sketch, "E209.MirrorCS", {"start": v(0, 139) * mm, "end": v(0, 130) * mm, "construction": true});
            skLineSegment(sketch, "E210.MirrorCS", {"start": v(-12.26, 140.03) * mm, "end": v(23.38, 137.03) * mm});
            skLineSegment(sketch, "E211.MirrorCS", {"start": v(-27.5, 250) * mm, "end": v(-27.5, 130) * mm});
            skArc(sketch, "E212.MirrorCS", {"start": v(-20.5, 231) * mm, "mid": v(-18.13, 237.1) * mm, "end": v(-12.26, 239.97) * mm});
            skLineSegment(sketch, "E213.MirrorCS", {"start": v(-27.5, 130) * mm, "end": v(27.5, 130) * mm});
            skArc(sketch, "E214.MirrorCS", {"start": v(-12.26, 140.03) * mm, "mid": v(-18.13, 142.9) * mm, "end": v(-20.5, 149) * mm});
            skLineSegment(sketch, "E215.MirrorCS", {"start": v(27.5, 250) * mm, "end": v(-27.5, 250) * mm});
            skLineSegment(sketch, "E216.MirrorCS", {"start": v(-20.5, 190) * mm, "end": v(-27.5, 190) * mm});
            skLineSegment(sketch, "E217.MirrorCS", {"start": v(-20.5, 231) * mm, "end": v(-20.5, 149) * mm});
            skPoint(sketch, "E218.MirrorP", {"position": v(27.5, 243.32) * mm});
            skPoint(sketch, "E219.MirrorP", {"position": v(27.5, 136.68) * mm});
            skPoint(sketch, "E220.MirrorP", {"position": v(-20.5, 140.73) * mm});
            skLineSegment(sketch, "E221.MirrorCS", {"start": v(0, 800) * mm, "end": v(0, -101.35) * mm, "construction": true});
            skPoint(sketch, "E222.MirrorP", {"position": v(-20.5, 239.27) * mm});
            skPoint(sketch, "E223.MirrorP", {"position": v(-27.5, 190) * mm});
            skSolve(sketch);
        }
        {
            var Q0;
            Q0 = qSketchRegion(id + "F10", true);
            var Q1;
            Q1=makeQuery(id+"F1.opExtrude","SWEPT_FACE",FACE,{"disambiguationData":[OSD([sQuery(id+"F0.wireOp",EDGE,"E77.MirrorCS")])]});
            extrude(context, id + "F11", {"entities" : qUnion([Q0]), "endBound" : BoundingType.UP_TO_SURFACE, "endBoundEntityFace" : qUnion([Q1]), "depth" : 25 * mm});
        }
        {
            var Q0;
            Q0=makeQuery(id+"F1.opExtrude","SWEPT_FACE",FACE,{"disambiguationData":[OSD([sQuery(id+"F0.wireOp",EDGE,"E83.MirrorCS")])]});
            var sketch = newSketch(context, id + "F12", { "sketchPlane" : qUnion([Q0])});
            skLineSegment(sketch, "E224", {"start": v(1222.5, 250) * mm, "end": v(1277.5, 250) * mm});
            skLineSegment(sketch, "E225", {"start": v(1277.5, 250) * mm, "end": v(1277.5, 190) * mm});
            skLineSegment(sketch, "E226", {"start": v(1270.5, 190) * mm, "end": v(1270.5, 231) * mm});
            skLineSegment(sketch, "E227", {"start": v(1262.26, 239.97) * mm, "end": v(1226.62, 242.97) * mm});
            skLineSegment(sketch, "E228", {"start": v(1222.5, 247.45) * mm, "end": v(1222.5, 250) * mm});
            skLineSegment(sketch, "E229", {"start": v(1250, 250) * mm, "end": v(1250, 241) * mm, "construction": true});
            skPoint(sketch, "E230.visualSharp", {"position": v(1270.5, 239.27) * mm});
            skArc(sketch, "E230.filletArc", {"start": v(1270.5, 231) * mm, "mid": v(1268.13, 237.1) * mm, "end": v(1262.26, 239.97) * mm});
            skPoint(sketch, "E231.visualSharp", {"position": v(1222.5, 243.32) * mm});
            skArc(sketch, "E231.filletArc", {"start": v(1222.5, 247.45) * mm, "mid": v(1223.69, 244.4) * mm, "end": v(1226.62, 242.97) * mm});
            skLineSegment(sketch, "E232", {"start": v(1641.97, 190) * mm, "end": v(1277.5, 190) * mm, "construction": true});
            skLineSegment(sketch, "E233.MirrorCS", {"start": v(1222.5, 132.55) * mm, "end": v(1222.5, 130) * mm});
            skArc(sketch, "E234.MirrorCS", {"start": v(1222.5, 132.55) * mm, "mid": v(1223.69, 135.6) * mm, "end": v(1226.62, 137.03) * mm});
            skArc(sketch, "E235.MirrorCS", {"start": v(1270.5, 149) * mm, "mid": v(1268.13, 142.9) * mm, "end": v(1262.26, 140.03) * mm});
            skLineSegment(sketch, "E236.MirrorCS", {"start": v(1250, 130) * mm, "end": v(1250, 139) * mm, "construction": true});
            skPoint(sketch, "E237.MirrorP", {"position": v(1270.5, 140.73) * mm});
            skLineSegment(sketch, "E238.MirrorCS", {"start": v(1262.26, 140.03) * mm, "end": v(1226.62, 137.03) * mm});
            skLineSegment(sketch, "E239.MirrorCS", {"start": v(1270.5, 190) * mm, "end": v(1270.5, 149) * mm});
            skPoint(sketch, "E240.MirrorP", {"position": v(1222.5, 136.68) * mm});
            skLineSegment(sketch, "E241.MirrorCS", {"start": v(1277.5, 130) * mm, "end": v(1277.5, 190) * mm});
            skLineSegment(sketch, "E242.MirrorCS", {"start": v(1222.5, 130) * mm, "end": v(1277.5, 130) * mm});
            skLineSegment(sketch, "E243", {"start": v(1250, 800) * mm, "end": v(1250, -123.6) * mm, "construction": true});
            skLineSegment(sketch, "E244", {"start": v(0, 854.13) * mm, "end": v(0, -169.45) * mm, "construction": true});
            skLineSegment(sketch, "E245", {"start": v(0, 854.13) * mm, "end": v(1250, 854.13) * mm, "construction": true});
            skLineSegment(sketch, "E246", {"start": v(1250, 854.13) * mm, "end": v(1250, 800) * mm, "construction": true});
            skLineSegment(sketch, "E247", {"start": v(625, 854.13) * mm, "end": v(625, -232.4) * mm, "construction": true});
            skLineSegment(sketch, "E248.MirrorCS", {"start": v(0, 130) * mm, "end": v(0, 139) * mm, "construction": true});
            skArc(sketch, "E249.MirrorCS", {"start": v(27.5, 132.55) * mm, "mid": v(26.31, 135.6) * mm, "end": v(23.38, 137.03) * mm});
            skLineSegment(sketch, "E250.MirrorCS", {"start": v(27.5, 132.55) * mm, "end": v(27.5, 130) * mm});
            skLineSegment(sketch, "E251.MirrorCS", {"start": v(27.5, 247.45) * mm, "end": v(27.5, 250) * mm});
            skLineSegment(sketch, "E252.MirrorCS", {"start": v(-12.26, 140.03) * mm, "end": v(23.38, 137.03) * mm});
            skLineSegment(sketch, "E253.MirrorCS", {"start": v(0, 250) * mm, "end": v(0, 241) * mm, "construction": true});
            skLineSegment(sketch, "E254.MirrorCS", {"start": v(-20.5, 190) * mm, "end": v(-20.5, 149) * mm});
            skArc(sketch, "E255.MirrorCS", {"start": v(27.5, 247.45) * mm, "mid": v(26.31, 244.4) * mm, "end": v(23.38, 242.97) * mm});
            skArc(sketch, "E256.MirrorCS", {"start": v(-20.5, 149) * mm, "mid": v(-18.13, 142.9) * mm, "end": v(-12.26, 140.03) * mm});
            skLineSegment(sketch, "E257.MirrorCS", {"start": v(27.5, 130) * mm, "end": v(-27.5, 130) * mm});
            skLineSegment(sketch, "E258.MirrorCS", {"start": v(-27.5, 130) * mm, "end": v(-27.5, 190) * mm});
            skLineSegment(sketch, "E259.MirrorCS", {"start": v(27.5, 250) * mm, "end": v(-27.5, 250) * mm});
            skLineSegment(sketch, "E260.MirrorCS", {"start": v(-20.5, 190) * mm, "end": v(-20.5, 231) * mm});
            skArc(sketch, "E261.MirrorCS", {"start": v(-20.5, 231) * mm, "mid": v(-18.13, 237.1) * mm, "end": v(-12.26, 239.97) * mm});
            skLineSegment(sketch, "E262.MirrorCS", {"start": v(-12.26, 239.97) * mm, "end": v(23.38, 242.97) * mm});
            skLineSegment(sketch, "E263.MirrorCS", {"start": v(-27.5, 250) * mm, "end": v(-27.5, 190) * mm});
            skLineSegment(sketch, "E264.MirrorCS", {"start": v(-391.97, 190) * mm, "end": v(-27.5, 190) * mm, "construction": true});
            skLineSegment(sketch, "E265.MirrorCS", {"start": v(0, 800) * mm, "end": v(0, -123.6) * mm, "construction": true});
            skPoint(sketch, "E266.MirrorP", {"position": v(-20.5, 140.73) * mm});
            skPoint(sketch, "E267.MirrorP", {"position": v(27.5, 136.68) * mm});
            skPoint(sketch, "E268.MirrorP", {"position": v(-20.5, 239.27) * mm});
            skPoint(sketch, "E269.MirrorP", {"position": v(27.5, 243.32) * mm});
            skSolve(sketch);
        }
        {
            var Q0;
            Q0 = qSketchRegion(id + "F12", true);
            extrude(context, id + "F13", {"entities" : qUnion([Q0]), "endBound" : BoundingType.UP_TO_NEXT, "depth" : 25 * mm});
        }
        {
            var Q0;
            Q0=makeQuery(id+"F6.boolean.opBoolean","MERGE",FACE,{"derivedFrom":[makeQuery(id+"F1.opExtrude","SWEPT_FACE",FACE,{"disambiguationData":[OSD([sQuery(id+"F0.wireOp",EDGE,"E61.MirrorCS"),sQuery(id+"F0.wireOp",EDGE,"E64.MirrorCS")])]}),makeQuery(id+"F6.opExtrude","SWEPT_FACE",FACE,{"disambiguationData":[OSD([sQuery(id+"F5.wireOp",EDGE,"E169.bottom")])]})]});
            var sketch = newSketch(context, id + "F14", { "sketchPlane" : qUnion([Q0])});
            skLineSegment(sketch, "E270", {"start": v(-2518, 250) * mm, "end": v(-2573, 250) * mm});
            skLineSegment(sketch, "E271", {"start": v(-2573, 250) * mm, "end": v(-2573, 190) * mm});
            skLineSegment(sketch, "E272", {"start": v(-2566, 190) * mm, "end": v(-2566, 231) * mm});
            skLineSegment(sketch, "E273", {"start": v(-2557.76, 239.97) * mm, "end": v(-2522.12, 242.97) * mm});
            skLineSegment(sketch, "E274", {"start": v(-2518, 247.45) * mm, "end": v(-2518, 250) * mm});
            skPoint(sketch, "E275.visualSharp", {"position": v(-2566, 239.27) * mm});
            skArc(sketch, "E275.filletArc", {"start": v(-2557.76, 239.97) * mm, "mid": v(-2563.63, 237.1) * mm, "end": v(-2566, 231) * mm});
            skPoint(sketch, "E276.visualSharp", {"position": v(-2518, 243.32) * mm});
            skArc(sketch, "E276.filletArc", {"start": v(-2522.12, 242.97) * mm, "mid": v(-2519.19, 244.4) * mm, "end": v(-2518, 247.45) * mm});
            skLineSegment(sketch, "E277", {"start": v(-2545.5, 250) * mm, "end": v(-2545.5, 241) * mm, "construction": true});
            skLineSegment(sketch, "E278", {"start": v(-2649.47, 190) * mm, "end": v(-2573, 190) * mm, "construction": true});
            skArc(sketch, "E279.MirrorCS", {"start": v(-2522.12, 137.03) * mm, "mid": v(-2519.19, 135.6) * mm, "end": v(-2518, 132.55) * mm});
            skLineSegment(sketch, "E280.MirrorCS", {"start": v(-2518, 132.55) * mm, "end": v(-2518, 130) * mm});
            skArc(sketch, "E281.MirrorCS", {"start": v(-2557.76, 140.03) * mm, "mid": v(-2563.63, 142.9) * mm, "end": v(-2566, 149) * mm});
            skLineSegment(sketch, "E282.MirrorCS", {"start": v(-2545.5, 130) * mm, "end": v(-2545.5, 139) * mm, "construction": true});
            skLineSegment(sketch, "E283.MirrorCS", {"start": v(-2557.76, 140.03) * mm, "end": v(-2522.12, 137.03) * mm});
            skLineSegment(sketch, "E284.MirrorCS", {"start": v(-2573, 130) * mm, "end": v(-2573, 190) * mm});
            skPoint(sketch, "E285.MirrorP", {"position": v(-2566, 140.73) * mm});
            skLineSegment(sketch, "E286.MirrorCS", {"start": v(-2566, 190) * mm, "end": v(-2566, 149) * mm});
            skLineSegment(sketch, "E287.MirrorCS", {"start": v(-2518, 130) * mm, "end": v(-2573, 130) * mm});
            skPoint(sketch, "E288.MirrorP", {"position": v(-2518, 136.68) * mm});
            skLineSegment(sketch, "E289", {"start": v(-1256.5, 884.93) * mm, "end": v(-1256.5, -149.06) * mm, "construction": true});
            skLineSegment(sketch, "E290.MirrorCS", {"start": v(44.76, 239.97) * mm, "end": v(9.12, 242.97) * mm});
            skLineSegment(sketch, "E291.MirrorCS", {"start": v(5, 247.45) * mm, "end": v(5, 250) * mm});
            skLineSegment(sketch, "E292.MirrorCS", {"start": v(5, 132.55) * mm, "end": v(5, 130) * mm});
            skLineSegment(sketch, "E293.MirrorCS", {"start": v(44.76, 140.03) * mm, "end": v(9.12, 137.03) * mm});
            skLineSegment(sketch, "E294.MirrorCS", {"start": v(53, 190) * mm, "end": v(53, 231) * mm});
            skArc(sketch, "E295.MirrorCS", {"start": v(44.76, 239.97) * mm, "mid": v(50.63, 237.1) * mm, "end": v(53, 231) * mm});
            skArc(sketch, "E296.MirrorCS", {"start": v(9.12, 242.97) * mm, "mid": v(6.19, 244.4) * mm, "end": v(5, 247.45) * mm});
            skLineSegment(sketch, "E297.MirrorCS", {"start": v(32.5, 250) * mm, "end": v(32.5, 241) * mm, "construction": true});
            skArc(sketch, "E298.MirrorCS", {"start": v(9.12, 137.03) * mm, "mid": v(6.19, 135.6) * mm, "end": v(5, 132.55) * mm});
            skLineSegment(sketch, "E299.MirrorCS", {"start": v(5, 130) * mm, "end": v(60, 130) * mm});
            skArc(sketch, "E300.MirrorCS", {"start": v(44.76, 140.03) * mm, "mid": v(50.63, 142.9) * mm, "end": v(53, 149) * mm});
            skLineSegment(sketch, "E301.MirrorCS", {"start": v(32.5, 130) * mm, "end": v(32.5, 139) * mm, "construction": true});
            skLineSegment(sketch, "E302.MirrorCS", {"start": v(5, 250) * mm, "end": v(60, 250) * mm});
            skLineSegment(sketch, "E303.MirrorCS", {"start": v(53, 190) * mm, "end": v(53, 149) * mm});
            skLineSegment(sketch, "E304.MirrorCS", {"start": v(60, 250) * mm, "end": v(60, 190) * mm});
            skLineSegment(sketch, "E305.MirrorCS", {"start": v(60, 130) * mm, "end": v(60, 190) * mm});
            skLineSegment(sketch, "E306.MirrorCS", {"start": v(136.47, 190) * mm, "end": v(60, 190) * mm, "construction": true});
            skPoint(sketch, "E307.MirrorP", {"position": v(53, 239.27) * mm});
            skPoint(sketch, "E308.MirrorP", {"position": v(53, 140.73) * mm});
            skPoint(sketch, "E309.MirrorP", {"position": v(5, 243.32) * mm});
            skPoint(sketch, "E310.MirrorP", {"position": v(5, 136.68) * mm});
            skLineSegment(sketch, "E311", {"start": v(-1284, 251) * mm, "end": v(-1229, 251) * mm});
            skLineSegment(sketch, "E312", {"start": v(-1284, 251) * mm, "end": v(-1284, 191) * mm});
            skLineSegment(sketch, "E313", {"start": v(-1284, 191) * mm, "end": v(-822.78, 191) * mm, "construction": true});
            skLineSegment(sketch, "E314", {"start": v(-1229, 251) * mm, "end": v(-1229, 248.45) * mm});
            skLineSegment(sketch, "E315", {"start": v(-1233.12, 243.97) * mm, "end": v(-1268.76, 240.97) * mm});
            skLineSegment(sketch, "E316", {"start": v(-1277, 232) * mm, "end": v(-1277, 191) * mm});
            skPoint(sketch, "E317.visualSharp", {"position": v(-1229, 244.32) * mm});
            skArc(sketch, "E317.filletArc", {"start": v(-1233.12, 243.97) * mm, "mid": v(-1230.19, 245.4) * mm, "end": v(-1229, 248.45) * mm});
            skPoint(sketch, "E318.visualSharp", {"position": v(-1277, 240.27) * mm});
            skArc(sketch, "E318.filletArc", {"start": v(-1268.76, 240.97) * mm, "mid": v(-1274.63, 238.1) * mm, "end": v(-1277, 232) * mm});
            skLineSegment(sketch, "E319", {"start": v(-1256.5, 251) * mm, "end": v(-1256.5, 242) * mm, "construction": true});
            skLineSegment(sketch, "E320.MirrorCS", {"start": v(-1229, 131) * mm, "end": v(-1229, 133.55) * mm});
            skArc(sketch, "E321.MirrorCS", {"start": v(-1233.12, 138.03) * mm, "mid": v(-1230.19, 136.6) * mm, "end": v(-1229, 133.55) * mm});
            skLineSegment(sketch, "E322.MirrorCS", {"start": v(-1256.5, 131) * mm, "end": v(-1256.5, 140) * mm, "construction": true});
            skArc(sketch, "E323.MirrorCS", {"start": v(-1268.76, 141.03) * mm, "mid": v(-1274.63, 143.9) * mm, "end": v(-1277, 150) * mm});
            skLineSegment(sketch, "E324.MirrorCS", {"start": v(-1233.12, 138.03) * mm, "end": v(-1268.76, 141.03) * mm});
            skLineSegment(sketch, "E325.MirrorCS", {"start": v(-1277, 150) * mm, "end": v(-1277, 191) * mm});
            skPoint(sketch, "E326.MirrorP", {"position": v(-1229, 137.68) * mm});
            skLineSegment(sketch, "E327.MirrorCS", {"start": v(-1284, 131) * mm, "end": v(-1229, 131) * mm});
            skPoint(sketch, "E328.MirrorP", {"position": v(-1277, 141.73) * mm});
            skLineSegment(sketch, "E329.MirrorCS", {"start": v(-1284, 131) * mm, "end": v(-1284, 191) * mm});
            skSolve(sketch);
        }
        {
            var Q0;
            Q0 = qSketchRegion(id + "F14", true);
            extrude(context, id + "F15", {"entities" : qUnion([Q0]), "endBound" : BoundingType.UP_TO_NEXT, "depth" : 25 * mm});
        }
        {
            var Q0;
            Q0=makeQuery(id+"F1.opExtrude","CAP_FACE",FACE,{"disambiguationData":[OSD([sQuery(id+"F0.wireOp",EDGE,"E96.MirrorCS"),sQuery(id+"F0.wireOp",EDGE,"E98.MirrorCS"),sQuery(id+"F0.wireOp",EDGE,"E99.MirrorCS"),sQuery(id+"F0.wireOp",EDGE,"E102.MirrorCS"),sQuery(id+"F0.wireOp",EDGE,"E104.MirrorCS"),sQuery(id+"F0.wireOp",EDGE,"E106.MirrorCS"),sQuery(id+"F0.wireOp",EDGE,"E107.MirrorCS"),sQuery(id+"F0.wireOp",EDGE,"E109.MirrorCS"),sQuery(id+"F0.wireOp",EDGE,"E111.MirrorCS"),sQuery(id+"F0.wireOp",EDGE,"E113.MirrorCS"),sQuery(id+"F0.wireOp",EDGE,"E116.MirrorCS"),sQuery(id+"F0.wireOp",EDGE,"E117.MirrorCS"),sQuery(id+"F0.wireOp",EDGE,"E119.MirrorCS"),sQuery(id+"F0.wireOp",EDGE,"E120.MirrorCS"),sQuery(id+"F0.wireOp",EDGE,"E121.MirrorCS"),sQuery(id+"F0.wireOp",EDGE,"E124.MirrorCS"),sQuery(id+"F0.wireOp",EDGE,"E125.MirrorCS"),sQuery(id+"F0.wireOp",EDGE,"E126.MirrorCS")])],"isStart":false});
            var sketch = newSketch(context, id + "F16", { "sketchPlane" : qUnion([Q0])});
            skLineSegment(sketch, "E330.bottom", {"start": v(-2756.5, 243) * mm, "end": v(243.5, 243) * mm});
            skLineSegment(sketch, "E330.top", {"start": v(-2756.5, -1493) * mm, "end": v(243.5, -1493) * mm});
            skLineSegment(sketch, "E330.left", {"start": v(-2756.5, 243) * mm, "end": v(-2756.5, -1493) * mm});
            skLineSegment(sketch, "E330.right", {"start": v(243.5, 243) * mm, "end": v(243.5, -1493) * mm});
            skLineSegment(sketch, "E331", {"start": v(-1256.5, 243) * mm, "end": v(-1256.5, -1383.85) * mm, "construction": true});
            skSolve(sketch);
        }
        {
            var Q0;
            Q0 = qSketchRegion(id + "F16", true);
            extrude(context, id + "F17", {"entities" : qUnion([Q0]), "depth" : 60 * mm});
        }
    });
